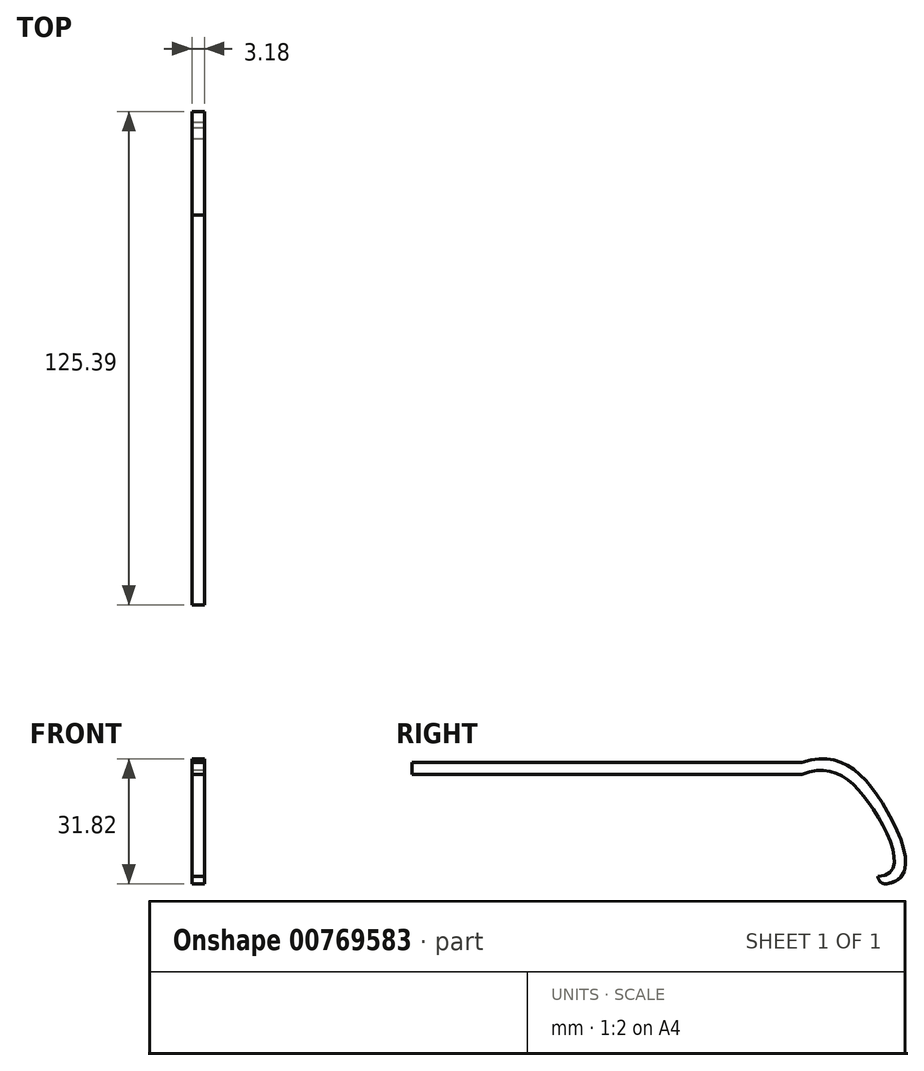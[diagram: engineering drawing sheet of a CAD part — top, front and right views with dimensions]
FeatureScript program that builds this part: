
annotation { "Feature Type Name" : "Feature", "Feature Type Description" : "" }
export const myFeature = defineFeature(function(context is Context, id is Id, definition is map)
    precondition{}
    {
        {
            var Q0;
            Q0=qCreatedBy(makeId("Right.planeOp"),FACE);
            var sketch = newSketch(context, id + "F0", { "sketchPlane" : qUnion([Q0])});
            skLineSegment(sketch, "E0", {"start": v(-57.49, 21.28) * mm, "end": v(41.57, 21.28) * mm});
            skLineSegment(sketch, "E1", {"start": v(-57.49, 21.28) * mm, "end": v(-57.49, 18.23) * mm});
            skLineSegment(sketch, "E2", {"start": v(-57.49, 18.23) * mm, "end": v(41.57, 18.23) * mm});
            skFitSpline(sketch, "E3", {"points": [v(41.57, 21.28) * mm, v(61.4, 11.82) * mm, v(63.68, -9.43) * mm], "startDerivative": vector(53.23, 17.75) * mm, "endDerivative": vector(-48.79, -9.5) * mm});
            skFitSpline(sketch, "E4", {"points": [v(41.57, 18.23) * mm, v(59.73, 9.28) * mm, v(60.88, -7.67) * mm], "startDerivative": vector(45.68, 18.07) * mm, "endDerivative": vector(-47.67, -1.6) * mm});
            skArc(sketch, "E5", {"start": v(60.88, -7.67) * mm, "mid": v(61.81, -9.3) * mm, "end": v(63.68, -9.43) * mm});
            skSolve(sketch);
        }
        {
            var Q0;
            Q0=makeQuery(id+"F0.imprint","IMPRINT",FACE,{"disambiguationData":[TD([[makeQuery(id+"F0.imprint","IMPRINT",EDGE,{"derivedFrom":sQuery(id+"F0.wireOp",EDGE,"E0")}),-1.0]])]});
            extrude(context, id + "F1", {"entities" : qUnion([Q0]), "depth" : 3.17 * mm, "offsetDistance" : 25.4 * mm});
        }
    });
